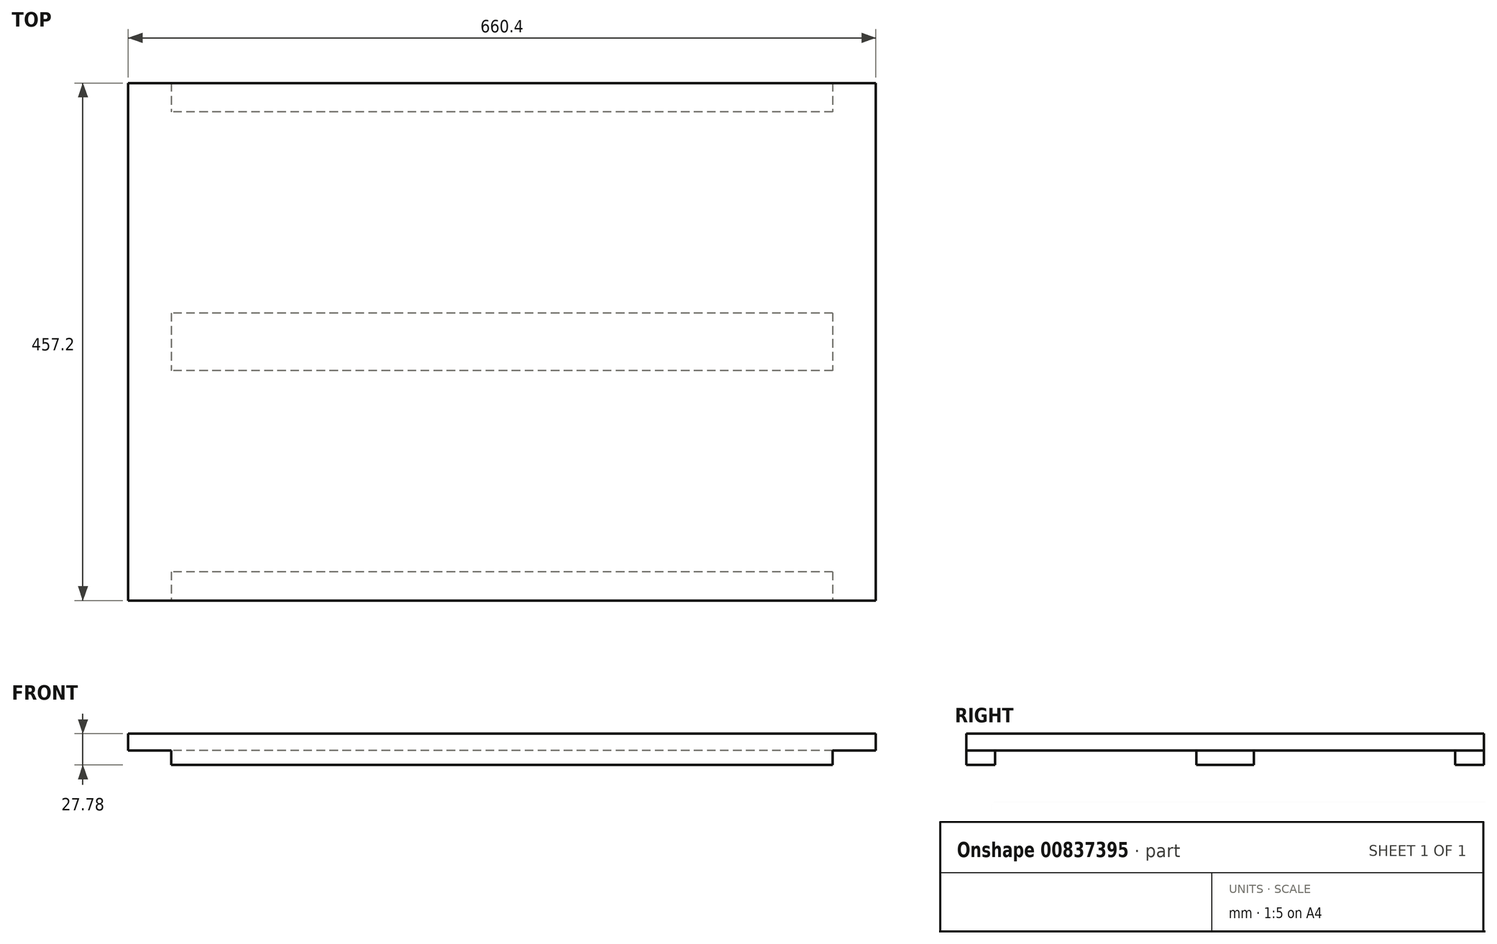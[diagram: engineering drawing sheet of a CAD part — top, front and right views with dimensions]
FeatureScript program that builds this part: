
annotation { "Feature Type Name" : "Feature", "Feature Type Description" : "" }
export const myFeature = defineFeature(function(context is Context, id is Id, definition is map)
    precondition{}
    {
        {
            var Q0;
            Q0=qCreatedBy(makeId("Right.planeOp"),FACE);
            var sketch = newSketch(context, id + "F0", { "sketchPlane" : qUnion([Q0])});
            skLineSegment(sketch, "E0.bottom", {"start": v(-228.6, 0) * mm, "end": v(228.6, 0) * mm});
            skLineSegment(sketch, "E0.top", {"start": v(-228.6, 15.08) * mm, "end": v(228.6, 15.08) * mm});
            skLineSegment(sketch, "E0.left", {"start": v(-228.6, 0) * mm, "end": v(-228.6, 15.08) * mm});
            skLineSegment(sketch, "E0.right", {"start": v(228.6, 0) * mm, "end": v(228.6, 15.08) * mm});
            skLineSegment(sketch, "E1.bottom", {"start": v(-228.6, 0) * mm, "end": v(-203.2, 0) * mm});
            skLineSegment(sketch, "E1.top", {"start": v(-228.6, -12.7) * mm, "end": v(-203.2, -12.7) * mm});
            skLineSegment(sketch, "E1.left", {"start": v(-228.6, 0) * mm, "end": v(-228.6, -12.7) * mm});
            skLineSegment(sketch, "E1.right", {"start": v(-203.2, 0) * mm, "end": v(-203.2, -12.7) * mm});
            skLineSegment(sketch, "E2.bottom", {"start": v(228.6, 0) * mm, "end": v(203.2, 0) * mm});
            skLineSegment(sketch, "E2.top", {"start": v(228.6, -12.7) * mm, "end": v(203.2, -12.7) * mm});
            skLineSegment(sketch, "E2.left", {"start": v(228.6, 0) * mm, "end": v(228.6, -12.7) * mm});
            skLineSegment(sketch, "E2.right", {"start": v(203.2, 0) * mm, "end": v(203.2, -12.7) * mm});
            skSolve(sketch);
        }
        {
            var Q0;
            Q0=makeQuery(id+"F0.imprint","IMPRINT",FACE,{"disambiguationData":[TD([[makeQuery(id+"F0.imprint","IMPRINT",EDGE,{"derivedFrom":sQuery(id+"F0.wireOp",EDGE,"E1.top")}),1.0]])]});
            var Q1;
            Q1=makeQuery(id+"F0.imprint","IMPRINT",FACE,{"disambiguationData":[TD([[makeQuery(id+"F0.imprint","IMPRINT",EDGE,{"derivedFrom":sQuery(id+"F0.wireOp",EDGE,"E0.top")}),-1.0]])]});
            var Q2;
            Q2=makeQuery(id+"F0.imprint","IMPRINT",FACE,{"disambiguationData":[TD([[makeQuery(id+"F0.imprint","IMPRINT",EDGE,{"derivedFrom":sQuery(id+"F0.wireOp",EDGE,"E2.top")}),-1.0]])]});
            extrude(context, id + "F1", {"entities" : qUnion([Q0, Q1, Q2]), "endBound" : BoundingType.SYMMETRIC, "depth" : 660.4 * mm, "offsetDistance" : 25.4 * mm});
        }
        {
            var Q0;
            Q0=makeQuery(id+"F1.opExtrude","SWEPT_FACE",FACE,{"disambiguationData":[OSD([sQuery(id+"F0.wireOp",EDGE,"E0.left"),sQuery(id+"F0.wireOp",EDGE,"E1.left")])]});
            var sketch = newSketch(context, id + "F2", { "sketchPlane" : qUnion([Q0])});
            skLineSegment(sketch, "E3.bottom", {"start": v(-330.2, -12.7) * mm, "end": v(-292.1, -12.7) * mm});
            skLineSegment(sketch, "E3.top", {"start": v(-330.2, 0) * mm, "end": v(-292.1, 0) * mm});
            skLineSegment(sketch, "E3.left", {"start": v(-330.2, -12.7) * mm, "end": v(-330.2, 0) * mm});
            skLineSegment(sketch, "E3.right", {"start": v(-292.1, -12.7) * mm, "end": v(-292.1, 0) * mm});
            skLineSegment(sketch, "E4.bottom", {"start": v(330.2, -12.7) * mm, "end": v(292.1, -12.7) * mm});
            skLineSegment(sketch, "E4.top", {"start": v(330.2, 0) * mm, "end": v(292.1, 0) * mm});
            skLineSegment(sketch, "E4.left", {"start": v(330.2, -12.7) * mm, "end": v(330.2, 0) * mm});
            skLineSegment(sketch, "E4.right", {"start": v(292.1, -12.7) * mm, "end": v(292.1, 0) * mm});
            skSolve(sketch);
        }
        {
            var Q0;
            Q0=makeQuery(id+"F2.imprint","IMPRINT",FACE,{"disambiguationData":[TD([[makeQuery(id+"F2.imprint","IMPRINT",EDGE,{"derivedFrom":sQuery(id+"F2.wireOp",EDGE,"E3.bottom")}),-1.0]])]});
            var Q1;
            Q1=makeQuery(id+"F2.imprint","IMPRINT",FACE,{"disambiguationData":[TD([[makeQuery(id+"F2.imprint","IMPRINT",EDGE,{"derivedFrom":sQuery(id+"F2.wireOp",EDGE,"E4.bottom")}),-1.0]])]});
            extrude(context, id + "F3", {"entities" : qUnion([Q0, Q1]), "operationType" : NewBodyOperationType.REMOVE, "endBound" : BoundingType.THROUGH_ALL, "oppositeDirection" : true, "depth" : 25.4 * mm, "offsetDistance" : 25.4 * mm});
        }
        {
            var Q0;
            Q0=makeQuery(id+"F3.boolean.opBoolean","COPY",FACE,{"disambiguationData":[TD([makeQuery(id+"F1.opExtrude","SWEPT_FACE",FACE,{"disambiguationData":[OSD([sQuery(id+"F0.wireOp",EDGE,"E2.top")])]})])],"derivedFrom":makeQuery(id+"F3.opExtrude","SWEPT_FACE",FACE,{"disambiguationData":[OSD([sQuery(id+"F2.wireOp",EDGE,"E3.right")])]})});
            var sketch = newSketch(context, id + "F4", { "sketchPlane" : qUnion([Q0])});
            skLineSegment(sketch, "E5.bottom", {"start": v(-25.4, 0) * mm, "end": v(25.4, 0) * mm});
            skLineSegment(sketch, "E5.top", {"start": v(-25.4, -12.7) * mm, "end": v(25.4, -12.7) * mm});
            skLineSegment(sketch, "E5.left", {"start": v(-25.4, 0) * mm, "end": v(-25.4, -12.7) * mm});
            skLineSegment(sketch, "E5.right", {"start": v(25.4, 0) * mm, "end": v(25.4, -12.7) * mm});
            skSolve(sketch);
        }
        {
            var Q0;
            Q0=makeQuery(id+"F4.imprint","IMPRINT",FACE,{"disambiguationData":[TD([[makeQuery(id+"F4.imprint","IMPRINT",EDGE,{"derivedFrom":sQuery(id+"F4.wireOp",EDGE,"E5.bottom")}),-1.0]])]});
            var Q1;
            Q1=makeQuery(id+"F3.boolean.opBoolean","COPY",FACE,{"disambiguationData":[TD([makeQuery(id+"F1.opExtrude","SWEPT_FACE",FACE,{"disambiguationData":[OSD([sQuery(id+"F0.wireOp",EDGE,"E2.top")])]})])],"derivedFrom":makeQuery(id+"F3.opExtrude","SWEPT_FACE",FACE,{"disambiguationData":[OSD([sQuery(id+"F2.wireOp",EDGE,"E4.right")])]})});
            extrude(context, id + "F5", {"entities" : qUnion([Q0]), "operationType" : NewBodyOperationType.ADD, "endBound" : BoundingType.UP_TO_SURFACE, "oppositeDirection" : true, "depth" : 25.4 * mm, "endBoundEntityFace" : qUnion([Q1]), "offsetDistance" : 25.4 * mm});
        }
    });
